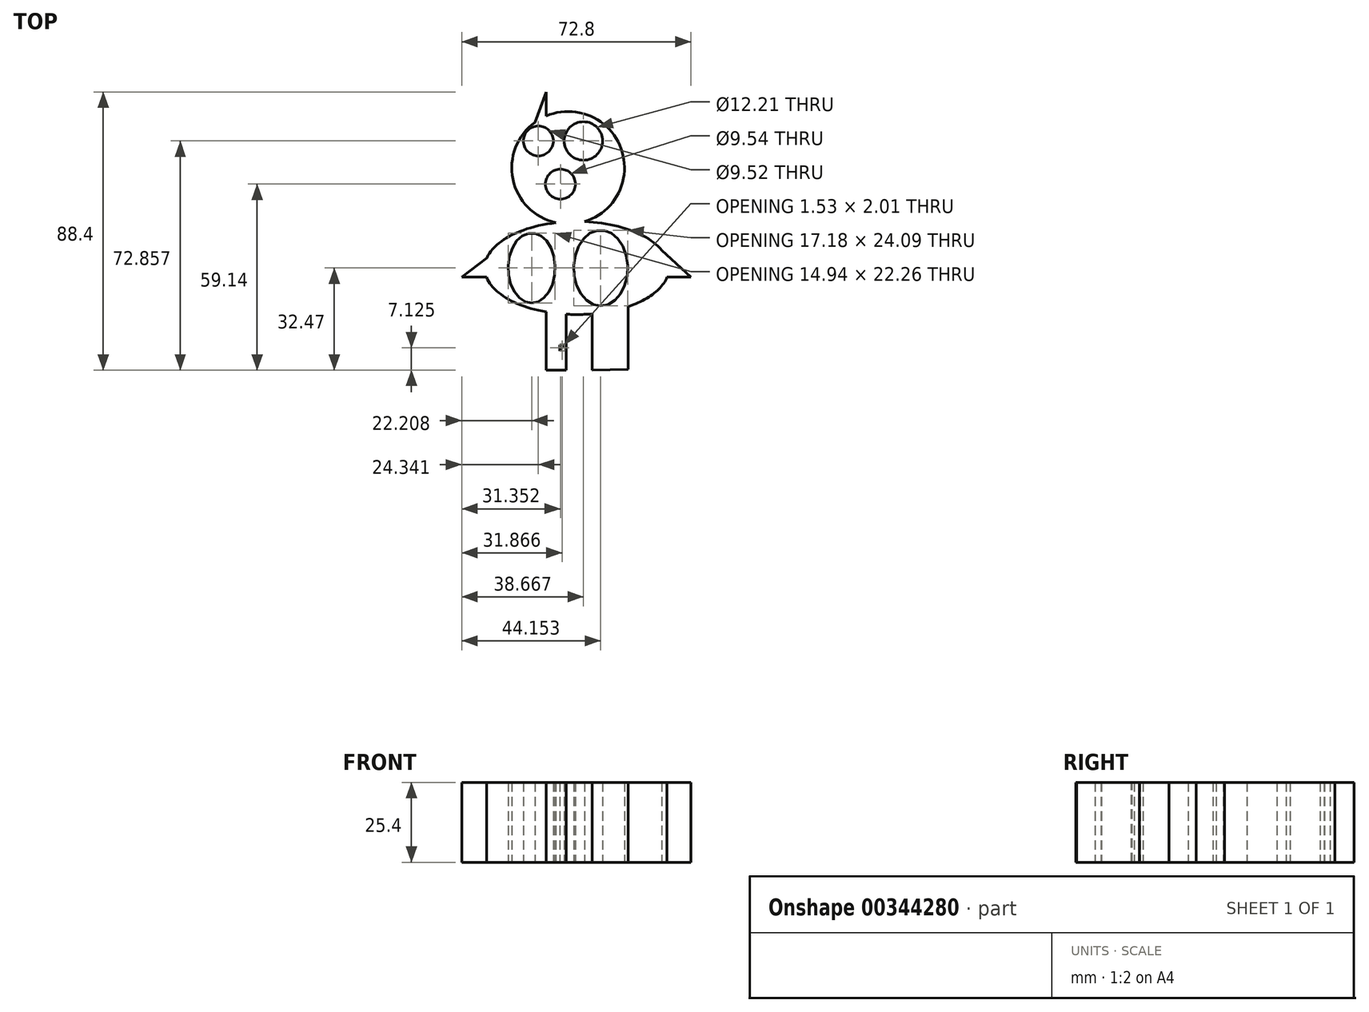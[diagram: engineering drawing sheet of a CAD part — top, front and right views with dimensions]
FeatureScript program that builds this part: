
annotation { "Feature Type Name" : "Feature", "Feature Type Description" : "" }
export const myFeature = defineFeature(function(context is Context, id is Id, definition is map)
    precondition{}
    {
        {
            var Q0;
            Q0=qCreatedBy(makeId("Top.planeOp"),FACE);
            var sketch = newSketch(context, id + "F0", { "sketchPlane" : qUnion([Q0])});
            skCircle(sketch, "E0", {"center": v(-7.62, 31.85) * mm, "radius": 17.9 * mm});
            skEllipse(sketch, "E1", {"center": v(-4.88, 0) * mm, "majorRadius": 29.26 * mm, "minorRadius": 14.79 * mm, "majorAxis": v(-1, 0)});
            skCircle(sketch, "E2", {"center": v(-17.07, 40.39) * mm, "radius": 4.76 * mm});
            skCircle(sketch, "E3", {"center": v(-2.74, 40.39) * mm, "radius": 6.1 * mm});
            skCircle(sketch, "E4", {"center": v(-10.06, 26.67) * mm, "radius": 4.77 * mm});
            skLineSegment(sketch, "E5", {"start": v(-33.41, 3.27) * mm, "end": v(-41.4, -2.92) * mm});
            skLineSegment(sketch, "E6", {"start": v(-41.4, -2.92) * mm, "end": v(-33.56, -2.92) * mm});
            skLineSegment(sketch, "E7", {"start": v(22.12, 5.7) * mm, "end": v(31.4, -2.92) * mm});
            skLineSegment(sketch, "E8", {"start": v(31.4, -2.92) * mm, "end": v(23.8, -2.92) * mm});
            skEllipse(sketch, "E9", {"center": v(-19.2, 0) * mm, "majorRadius": 11.13 * mm, "minorRadius": 7.47 * mm, "majorAxis": v(0, -1)});
            skEllipse(sketch, "E10", {"center": v(2.74, 0) * mm, "majorRadius": 12.04 * mm, "minorRadius": 8.59 * mm, "majorAxis": v(0, -1)});
            skLineSegment(sketch, "E11", {"start": v(-18.16, 46.32) * mm, "end": v(-14.63, 55.93) * mm});
            skLineSegment(sketch, "E12", {"start": v(-14.63, 55.93) * mm, "end": v(-14.63, 48.32) * mm});
            skLineSegment(sketch, "E13", {"start": v(-10.31, -24.47) * mm, "end": v(-10.31, -26.35) * mm});
            skLineSegment(sketch, "E14", {"start": v(-10.31, -24.47) * mm, "end": v(-8.78, -24.34) * mm});
            skLineSegment(sketch, "E15", {"start": v(-8.23, -23.63) * mm, "end": v(-10.31, -26.35) * mm});
            skPoint(sketch, "E16.start.orphan", {"position": v(-14.63, -13.94) * mm});
            skPoint(sketch, "E17.end.orphan", {"position": v(-4.21, -23.95) * mm});
            skPoint(sketch, "E17.start.orphan", {"position": v(-4.88, -14.79) * mm});
            skPoint(sketch, "E18.end.orphan", {"position": v(1.52, -23.95) * mm});
            skPoint(sketch, "E18.start.orphan", {"position": v(0, -14.58) * mm});
            skLineSegment(sketch, "E19", {"start": v(-14.63, -13.94) * mm, "end": v(-14.63, -32.47) * mm});
            skLineSegment(sketch, "E20", {"start": v(-8.23, -13.94) * mm, "end": v(-8.23, -32.47) * mm});
            skLineSegment(sketch, "E21", {"start": v(-8.23, -32.47) * mm, "end": v(-14.63, -32.47) * mm});
            skPoint(sketch, "E22.end.orphan", {"position": v(6.7, -14.58) * mm});
            skPoint(sketch, "E23.start.orphan", {"position": v(0, -32.47) * mm});
            skPoint(sketch, "E24.start.orphan", {"position": v(6.7, -32.47) * mm});
            skPoint(sketch, "E25.start.orphan", {"position": v(0, 48.32) * mm});
            skLineSegment(sketch, "E26", {"start": v(0, 48.32) * mm, "end": v(6.4, 56.24) * mm});
            skLineSegment(sketch, "E27", {"start": v(6.4, 56.24) * mm, "end": v(6.4, 42.98) * mm});
            skLineSegment(sketch, "E28", {"start": v(0, -14.58) * mm, "end": v(0, -32.47) * mm});
            skPoint(sketch, "E29.end.orphan", {"position": v(6.7, -23.95) * mm});
            skLineSegment(sketch, "E30", {"start": v(11.46, -12.27) * mm, "end": v(11.46, -32.18) * mm});
            skLineSegment(sketch, "E31", {"start": v(12.5, -32.16) * mm, "end": v(0, -32.47) * mm});
            skSolve(sketch);
        }
        {
            var Q0;
            Q0 = qSketchRegion(id + "F0", true);
            extrude(context, id + "F1", {"entities" : qUnion([Q0]), "depth" : 25.4 * mm});
        }
    });
